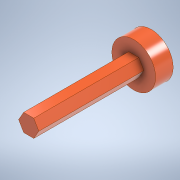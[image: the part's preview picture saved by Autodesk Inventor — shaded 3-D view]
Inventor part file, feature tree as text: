
AUTODESK INVENTOR PART (.ipt)
format: ipt  version: 2021.2 (Build 252289000, 289)  size: 116,736 bytes
history: native  units: in
note: dims shown in document units (in); Inventor stores cm internally (conversion verified against a paired STEP export)
features: extrude x2, sketch x2
ambient origin geometry x8: Origin, YZ Plane, XZ Plane, XY Plane, X Axis, Y Axis, Z Axis, Center Point
bodies: Solid1 (feature_tree)
feature tree (4):
  extrude  "Extrusion1"  Depth=3.0in TaperAngle=0.0deg
  extrude  "Extrusion2"  Depth=0.5in TaperAngle=0.0deg
  sketch  "Sketch1"  dims[d0=0.5in d1=3.0in d2=0.0in]
  sketch  "Sketch2"  dims[d3=1.25in d4=0.5in d5=0.0in]
